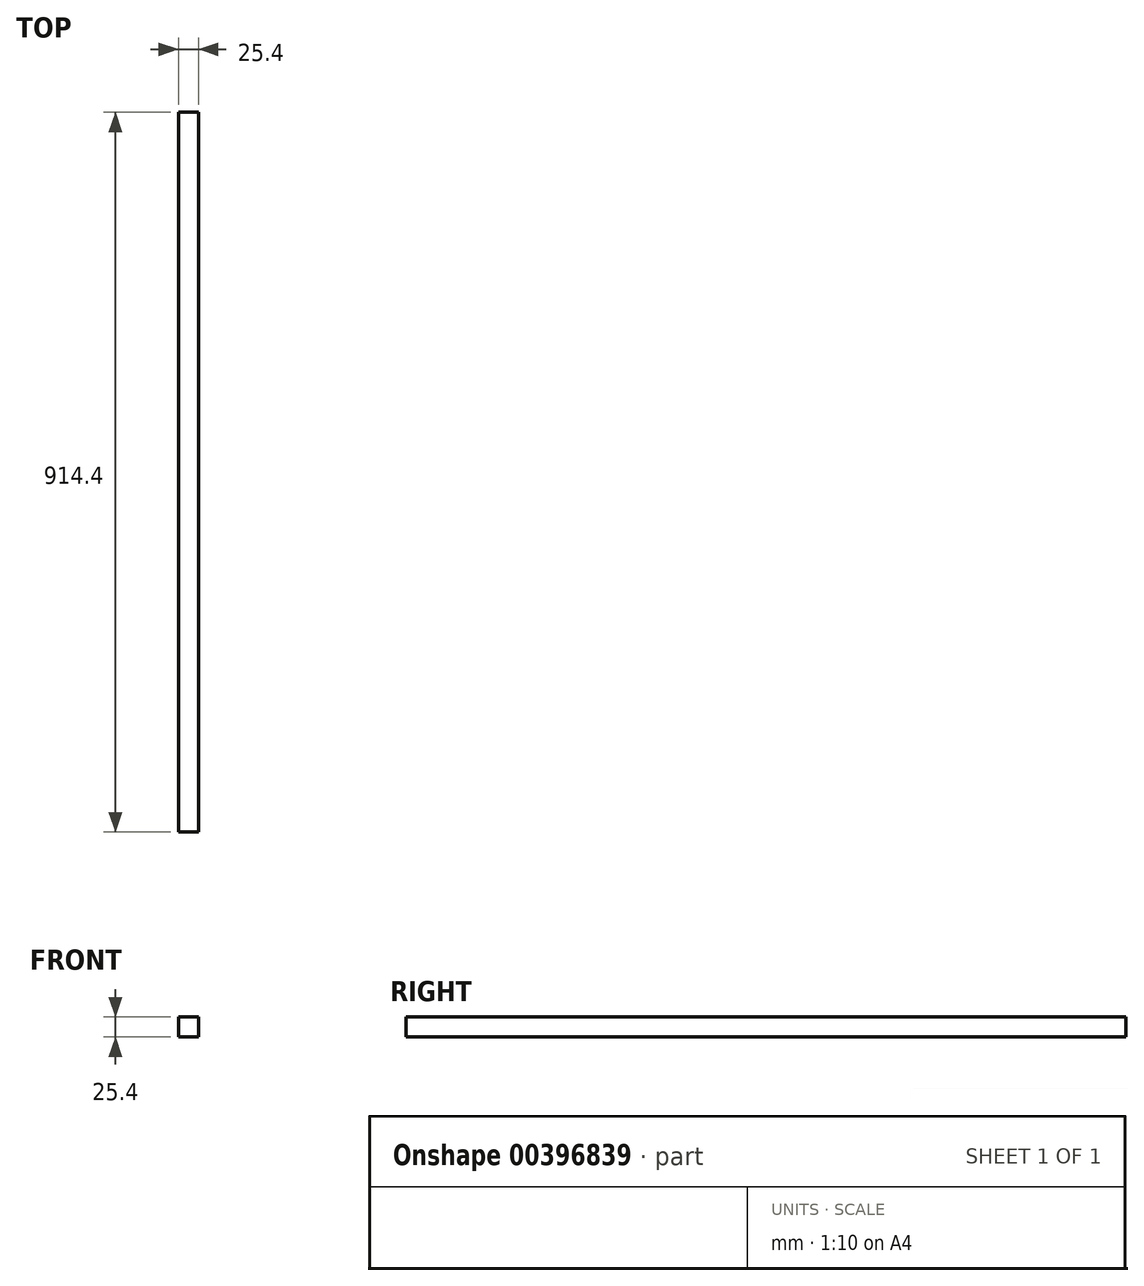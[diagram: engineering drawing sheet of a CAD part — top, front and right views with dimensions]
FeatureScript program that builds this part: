
annotation { "Feature Type Name" : "Feature", "Feature Type Description" : "" }
export const myFeature = defineFeature(function(context is Context, id is Id, definition is map)
    precondition{}
    {
        {
            var Q0;
            Q0=qCreatedBy(makeId("Top.planeOp"),FACE);
            var sketch = newSketch(context, id + "F0", { "sketchPlane" : qUnion([Q0])});
            skLineSegment(sketch, "E0.bottom", {"start": v(-12.7, 457.2) * mm, "end": v(12.7, 457.2) * mm});
            skLineSegment(sketch, "E0.top", {"start": v(-12.7, -457.2) * mm, "end": v(12.7, -457.2) * mm});
            skLineSegment(sketch, "E0.left", {"start": v(-12.7, 457.2) * mm, "end": v(-12.7, -457.2) * mm});
            skLineSegment(sketch, "E0.right", {"start": v(12.7, 457.2) * mm, "end": v(12.7, -457.2) * mm});
            skPoint(sketch, "E0.middle", {"position": v(0, 0) * mm});
            skSolve(sketch);
        }
        {
            var Q0;
            Q0=makeQuery(id+"F0.imprint","IMPRINT",FACE,{"disambiguationData":[TD([[makeQuery(id+"F0.imprint","IMPRINT",EDGE,{"derivedFrom":sQuery(id+"F0.wireOp",EDGE,"E0.bottom")}),-1.0]])]});
            extrude(context, id + "F1", {"entities" : qUnion([Q0]), "depth" : 25.4 * mm});
        }
    });
